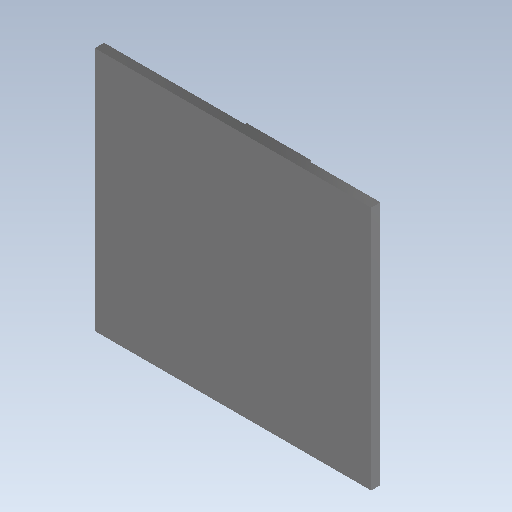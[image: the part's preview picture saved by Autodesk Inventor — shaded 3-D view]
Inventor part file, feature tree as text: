
AUTODESK INVENTOR PART (.ipt)
format: ipt  version: 2021.3 (Build 253353000, 353)  size: 143,360 bytes
history: native  units: mm
features: extrude x5, sketch x4, thread x2
ambient origin geometry x8: Origin, YZ Plane, XZ Plane, XY Plane, X Axis, Y Axis, Z Axis, Center Point
bodies: Solid1 (feature_tree)
feature tree (11):
  extrude  "Extrusion1"  Depth=266.0mm
  sketch  "Sketch2"  dims[d2=10.0mm d3=0.0mm d4=70.0mm]
  extrude  "Extrusion2"  Depth=70.0mm
  extrude  "Extrusion3"  Depth=70.0mm
  extrude  "Extrusion4"  Depth=30.0mm
  extrude  "Extrusion5"  Depth=30.0mm
  thread  "Thread1"  [1 undecoded]
  thread  "Thread2"  [1 undecoded]
  sketch  "Sketch1"  dims[d0=300.0mm d1=266.0mm]
  sketch  "Sketch3"  dims[d5=14.0mm d6=0.0mm d7=70.0mm]
  sketch  "Sketch4"  dims[d8=30.0mm d9=30.0mm d10=30.0mm d11=30.0mm d12=40.0mm d13=0.0mm d14=16.0mm d15=15.0mm d16=20.0mm d17=40.0mm d18=0.0mm d19=16.0mm d20=15.0mm d21=20.0mm d22=40.0mm d23=0.0mm d24=10.0mm d25=0.0mm d26=10.0mm d27=0.0mm]
note: 2 required parameter values undecoded (feature->parameter linkage not recoverable at this tier; creation-order binding heuristic only, values carry confidence <= 0.55)
